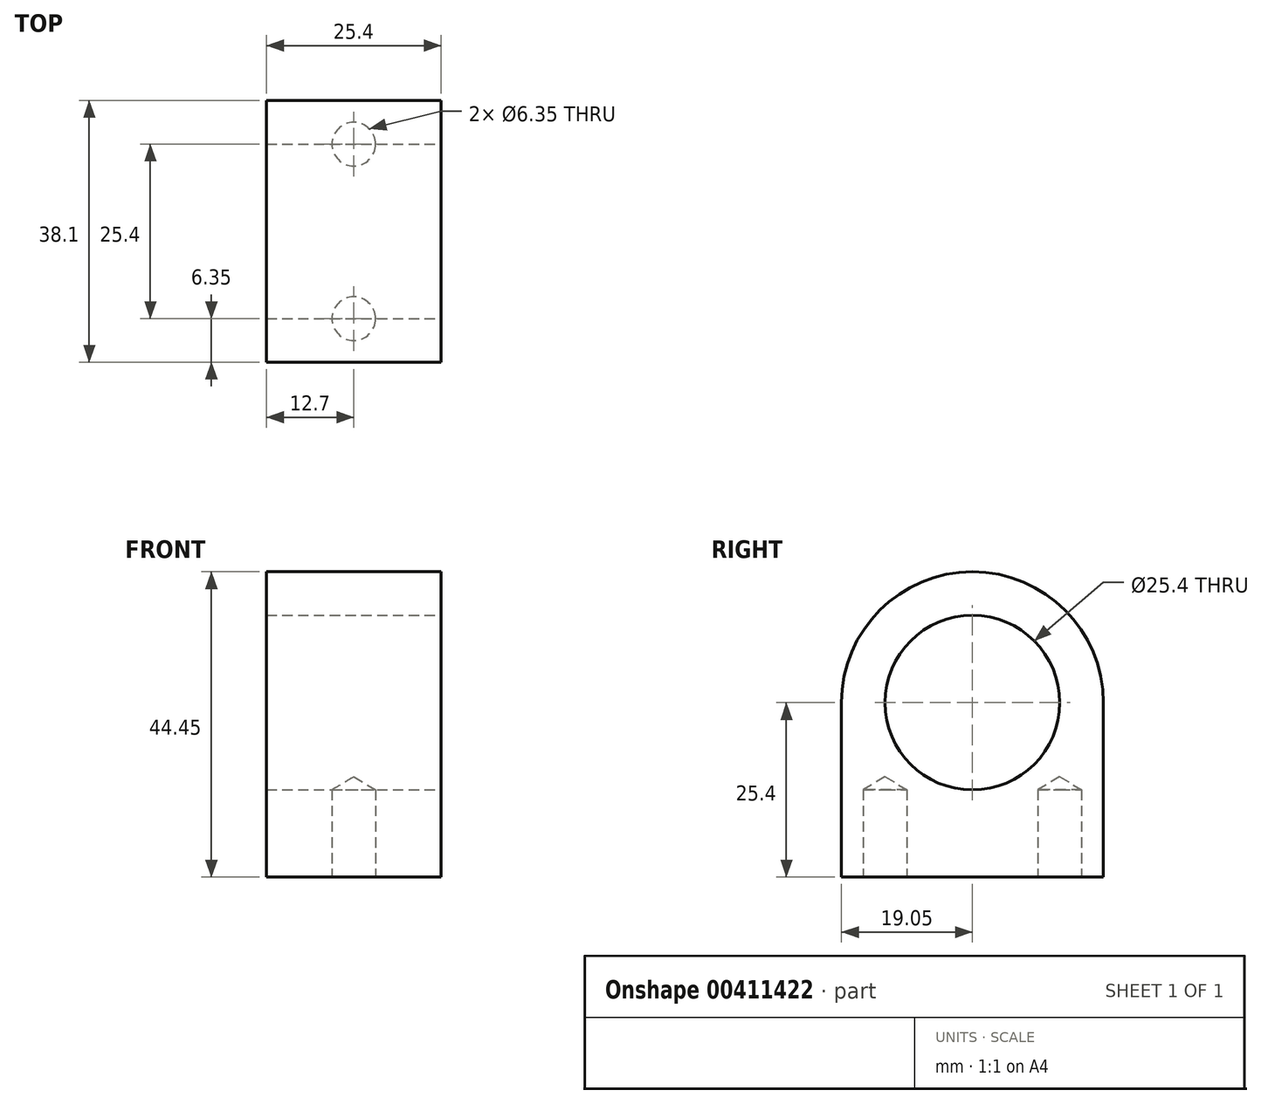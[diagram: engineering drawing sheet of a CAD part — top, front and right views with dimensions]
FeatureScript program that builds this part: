
annotation { "Feature Type Name" : "Feature", "Feature Type Description" : "" }
export const myFeature = defineFeature(function(context is Context, id is Id, definition is map)
    precondition{}
    {
        {
            var Q0;
            Q0=qCreatedBy(makeId("Right.planeOp"),FACE);
            var sketch = newSketch(context, id + "F0", { "sketchPlane" : qUnion([Q0])});
            skLineSegment(sketch, "E0", {"start": v(-19.05, -25.4) * mm, "end": v(19.05, -25.4) * mm});
            skLineSegment(sketch, "E1", {"start": v(19.05, -25.4) * mm, "end": v(19.05, 0) * mm});
            skLineSegment(sketch, "E2", {"start": v(-19.05, -25.4) * mm, "end": v(-19.05, 0) * mm});
            skArc(sketch, "E3", {"start": v(-19.05, 0) * mm, "mid": v(0, 19.05) * mm, "end": v(19.05, 0) * mm});
            skSolve(sketch);
        }
        {
            var Q0;
            Q0 = qSketchRegion(id + "F0", true);
            extrude(context, id + "F1", {"entities" : qUnion([Q0]), "endBound" : BoundingType.SYMMETRIC, "depth" : 25.4 * mm});
        }
        {
            var Q0;
            Q0=makeQuery(id+"F1.opExtrude","CAP_FACE",FACE,{"disambiguationData":[OSD([sQuery(id+"F0.wireOp",EDGE,"E0"),sQuery(id+"F0.wireOp",EDGE,"E1"),sQuery(id+"F0.wireOp",EDGE,"E2"),sQuery(id+"F0.wireOp",EDGE,"E3")])],"isStart":false});
            var sketch = newSketch(context, id + "F2", { "sketchPlane" : qUnion([Q0])});
            skCircle(sketch, "E4", {"center": v(0, 0) * mm, "radius": 12.7 * mm});
            skSolve(sketch);
        }
        {
            var Q0;
            Q0 = qSketchRegion(id + "F2", true);
            extrude(context, id + "F3", {"entities" : qUnion([Q0]), "operationType" : NewBodyOperationType.REMOVE, "endBound" : BoundingType.THROUGH_ALL, "oppositeDirection" : true, "depth" : 68.33 * mm});
        }
        {
            var Q0;
            Q0=makeQuery(id+"F1.opExtrude","SWEPT_FACE",FACE,{"disambiguationData":[OSD([sQuery(id+"F0.wireOp",EDGE,"E0")])]});
            var sketch = newSketch(context, id + "F4", { "sketchPlane" : qUnion([Q0])});
            skLineSegment(sketch, "E5", {"start": v(0, 19.05) * mm, "end": v(0, -19.05) * mm, "construction": true});
            skCircle(sketch, "E6", {"center": v(0, 12.7) * mm, "radius": 3.18 * mm});
            skCircle(sketch, "E7", {"center": v(0, -12.7) * mm, "radius": 3.18 * mm});
            skSolve(sketch);
        }
        {
            var Q0;
            Q0=sQuery(id+"F4.wireOp",VERTEX,"E6.center");
            var Q1;
            Q1=sQuery(id+"F4.wireOp",VERTEX,"E7.center");
            var Q2;
            Q2=makeQuery(id+"F1.opExtrude","SWEPT_BODY",BODY,{"disambiguationData":[OSD([sQuery(id+"F0.wireOp",EDGE,"E0"),sQuery(id+"F0.wireOp",EDGE,"E1"),sQuery(id+"F0.wireOp",EDGE,"E2"),sQuery(id+"F0.wireOp",EDGE,"E3")])]});
            hole(context, id + "F5", {"style" : HoleStyle.SIMPLE, "endStyle" : HoleEndStyle.BLIND, "holeDiameter" : 6.35 * mm, "holeDepth" : 12.7 * mm, "isTappedThrough" : true, "tappedDepth" : 12.7 * mm, "tapClearance" : 3, "locations" : qUnion([Q0, Q1]), "scope" : qUnion([Q2])});
        }
    });
